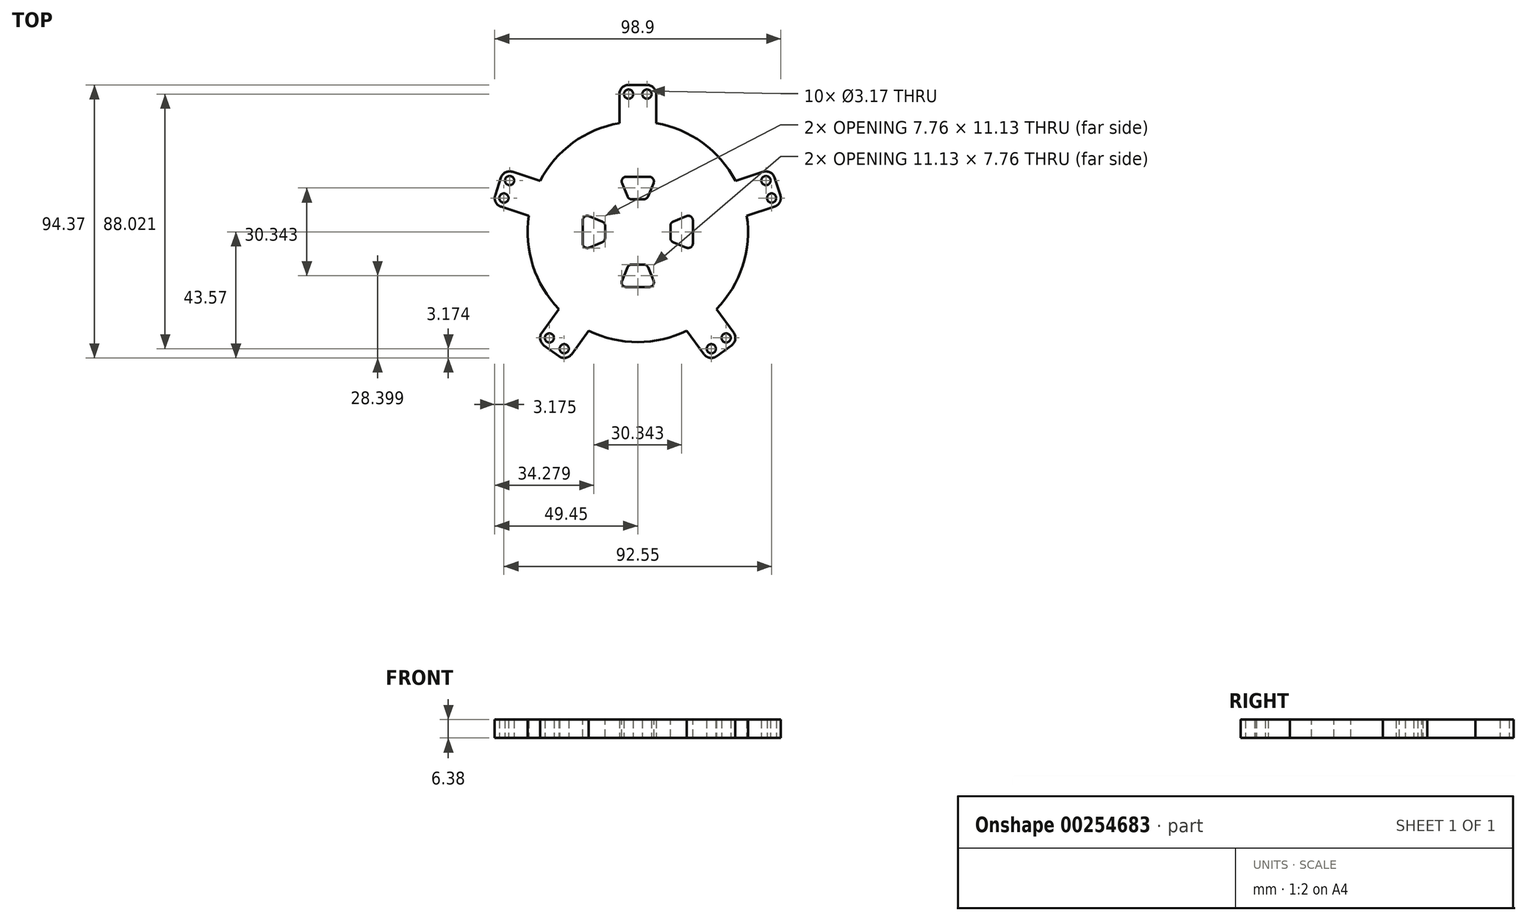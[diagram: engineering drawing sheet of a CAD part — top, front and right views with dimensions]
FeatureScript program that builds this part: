
annotation { "Feature Type Name" : "Feature", "Feature Type Description" : "" }
export const myFeature = defineFeature(function(context is Context, id is Id, definition is map)
    precondition{}
    {
        {
            var Q0;
            Q0=qCreatedBy(makeId("Top.planeOp"),FACE);
            var sketch = newSketch(context, id + "F0", { "sketchPlane" : qUnion([Q0])});
            skArc(sketch, "E0", {"start": v(-6.35, 37.57) * mm, "mid": v(-22.4, 30.82) * mm, "end": v(-33.77, 17.65) * mm});
            skLineSegment(sketch, "E1", {"start": v(0, 0) * mm, "end": v(0, 66.93) * mm, "construction": true});
            skLineSegment(sketch, "E2", {"start": v(-6.35, 37.57) * mm, "end": v(-6.35, 47.63) * mm});
            skLineSegment(sketch, "E3.MirrorCS", {"start": v(6.35, 37.57) * mm, "end": v(6.35, 47.63) * mm});
            skLineSegment(sketch, "E4", {"start": v(-3.18, 50.8) * mm, "end": v(3.18, 50.8) * mm});
            skCircle(sketch, "E5", {"center": v(-3.18, 47.63) * mm, "radius": 1.59 * mm});
            skCircle(sketch, "E6.MirrorC", {"center": v(3.18, 47.63) * mm, "radius": 1.59 * mm});
            skPoint(sketch, "E7.visualSharp", {"position": v(6.35, 50.8) * mm});
            skArc(sketch, "E7.filletArc", {"start": v(6.35, 47.63) * mm, "mid": v(5.42, 49.87) * mm, "end": v(3.18, 50.8) * mm});
            skPoint(sketch, "E8.visualSharp", {"position": v(-6.35, 50.8) * mm});
            skArc(sketch, "E8.filletArc", {"start": v(-3.18, 50.8) * mm, "mid": v(-5.42, 49.87) * mm, "end": v(-6.35, 47.63) * mm});
            skLineSegment(sketch, "E9.1.0", {"start": v(0, 0) * mm, "end": v(-63.65, 20.68) * mm, "construction": true});
            skLineSegment(sketch, "E9.1.1", {"start": v(-33.77, 17.65) * mm, "end": v(-43.33, 20.76) * mm});
            skPoint(sketch, "E9.1.2", {"position": v(-50.28, 9.66) * mm});
            skLineSegment(sketch, "E9.1.3", {"start": v(-49.3, 12.68) * mm, "end": v(-47.33, 18.72) * mm});
            skLineSegment(sketch, "E9.1.4", {"start": v(-37.7, 5.57) * mm, "end": v(-47.26, 8.68) * mm});
            skPoint(sketch, "E9.1.5", {"position": v(-46.35, 21.74) * mm});
            skArc(sketch, "E9.1.6", {"start": v(-43.33, 20.76) * mm, "mid": v(-45.75, 20.57) * mm, "end": v(-47.33, 18.72) * mm});
            skCircle(sketch, "E9.1.7", {"center": v(-44.31, 17.74) * mm, "radius": 1.59 * mm});
            skCircle(sketch, "E9.1.8", {"center": v(-46.28, 11.7) * mm, "radius": 1.59 * mm});
            skArc(sketch, "E9.1.9", {"start": v(-49.3, 12.68) * mm, "mid": v(-49.1, 10.26) * mm, "end": v(-47.26, 8.68) * mm});
            skLineSegment(sketch, "E9.2.0", {"start": v(0, 0) * mm, "end": v(-39.34, -54.15) * mm, "construction": true});
            skLineSegment(sketch, "E9.2.1", {"start": v(-27.22, -26.66) * mm, "end": v(-33.13, -34.8) * mm});
            skPoint(sketch, "E9.2.2", {"position": v(-24.72, -44.83) * mm});
            skLineSegment(sketch, "E9.2.3", {"start": v(-27.3, -42.96) * mm, "end": v(-32.43, -39.23) * mm});
            skLineSegment(sketch, "E9.2.4", {"start": v(-16.94, -34.12) * mm, "end": v(-22.86, -42.26) * mm});
            skPoint(sketch, "E9.2.5", {"position": v(-35, -37.37) * mm});
            skArc(sketch, "E9.2.6", {"start": v(-33.13, -34.8) * mm, "mid": v(-33.7, -37.16) * mm, "end": v(-32.43, -39.23) * mm});
            skCircle(sketch, "E9.2.7", {"center": v(-30.56, -36.66) * mm, "radius": 1.59 * mm});
            skCircle(sketch, "E9.2.8", {"center": v(-25.42, -40.4) * mm, "radius": 1.59 * mm});
            skArc(sketch, "E9.2.9", {"start": v(-27.3, -42.96) * mm, "mid": v(-24.93, -43.53) * mm, "end": v(-22.86, -42.26) * mm});
            skLineSegment(sketch, "E9.3.0", {"start": v(0, 0) * mm, "end": v(39.34, -54.15) * mm, "construction": true});
            skLineSegment(sketch, "E9.3.1", {"start": v(16.94, -34.12) * mm, "end": v(22.86, -42.26) * mm});
            skPoint(sketch, "E9.3.2", {"position": v(35, -37.37) * mm});
            skLineSegment(sketch, "E9.3.3", {"start": v(32.43, -39.23) * mm, "end": v(27.3, -42.96) * mm});
            skLineSegment(sketch, "E9.3.4", {"start": v(27.22, -26.66) * mm, "end": v(33.13, -34.8) * mm});
            skPoint(sketch, "E9.3.5", {"position": v(24.72, -44.83) * mm});
            skArc(sketch, "E9.3.6", {"start": v(22.86, -42.26) * mm, "mid": v(24.93, -43.53) * mm, "end": v(27.3, -42.96) * mm});
            skCircle(sketch, "E9.3.7", {"center": v(25.42, -40.4) * mm, "radius": 1.59 * mm});
            skCircle(sketch, "E9.3.8", {"center": v(30.56, -36.66) * mm, "radius": 1.59 * mm});
            skArc(sketch, "E9.3.9", {"start": v(32.43, -39.23) * mm, "mid": v(33.7, -37.16) * mm, "end": v(33.13, -34.8) * mm});
            skLineSegment(sketch, "E9.4.0", {"start": v(0, 0) * mm, "end": v(63.65, 20.68) * mm, "construction": true});
            skLineSegment(sketch, "E9.4.1", {"start": v(37.7, 5.57) * mm, "end": v(47.26, 8.68) * mm});
            skPoint(sketch, "E9.4.2", {"position": v(46.35, 21.74) * mm});
            skLineSegment(sketch, "E9.4.3", {"start": v(47.33, 18.72) * mm, "end": v(49.3, 12.68) * mm});
            skLineSegment(sketch, "E9.4.4", {"start": v(33.77, 17.65) * mm, "end": v(43.33, 20.76) * mm});
            skPoint(sketch, "E9.4.5", {"position": v(50.28, 9.66) * mm});
            skArc(sketch, "E9.4.6", {"start": v(47.26, 8.68) * mm, "mid": v(49.1, 10.26) * mm, "end": v(49.3, 12.68) * mm});
            skCircle(sketch, "E9.4.7", {"center": v(46.28, 11.7) * mm, "radius": 1.59 * mm});
            skCircle(sketch, "E9.4.8", {"center": v(44.31, 17.74) * mm, "radius": 1.59 * mm});
            skArc(sketch, "E9.4.9", {"start": v(47.33, 18.72) * mm, "mid": v(45.75, 20.57) * mm, "end": v(43.33, 20.76) * mm});
            skArc(sketch, "E10.trimOffspring", {"start": v(-37.7, 5.57) * mm, "mid": v(-36.24, -11.77) * mm, "end": v(-27.22, -26.66) * mm});
            skArc(sketch, "E11.trimOffspring", {"start": v(-16.94, -34.12) * mm, "mid": v(0, -38.1) * mm, "end": v(16.94, -34.12) * mm});
            skArc(sketch, "E12.trimOffspring", {"start": v(27.22, -26.66) * mm, "mid": v(36.24, -11.77) * mm, "end": v(37.7, 5.57) * mm});
            skArc(sketch, "E13.trimOffspring", {"start": v(33.77, 17.65) * mm, "mid": v(22.4, 30.82) * mm, "end": v(6.35, 37.57) * mm});
            skSolve(sketch);
        }
        {
            var Q0;
            Q0=makeQuery(id+"F0.imprint","IMPRINT",FACE,{"disambiguationData":[TD([[makeQuery(id+"F0.imprint","IMPRINT",EDGE,{"derivedFrom":sQuery(id+"F0.wireOp",EDGE,"E0")}),1.0]])]});
            extrude(context, id + "F1", {"entities" : qUnion([Q0]), "depth" : 6.38 * mm});
        }
        {
            var Q0;
            Q0=makeQuery(id+"F1.opExtrude","CAP_FACE",FACE,{"disambiguationData":[OSD([sQuery(id+"F0.wireOp",EDGE,"E0"),sQuery(id+"F0.wireOp",EDGE,"E2"),sQuery(id+"F0.wireOp",EDGE,"E3.MirrorCS"),sQuery(id+"F0.wireOp",EDGE,"E4"),sQuery(id+"F0.wireOp",EDGE,"E5"),sQuery(id+"F0.wireOp",EDGE,"E6.MirrorC"),sQuery(id+"F0.wireOp",EDGE,"E7.filletArc"),sQuery(id+"F0.wireOp",EDGE,"E8.filletArc"),sQuery(id+"F0.wireOp",EDGE,"E9.1.1"),sQuery(id+"F0.wireOp",EDGE,"E9.1.3"),sQuery(id+"F0.wireOp",EDGE,"E9.1.4"),sQuery(id+"F0.wireOp",EDGE,"E9.1.6"),sQuery(id+"F0.wireOp",EDGE,"E9.1.7"),sQuery(id+"F0.wireOp",EDGE,"E9.1.8"),sQuery(id+"F0.wireOp",EDGE,"E9.1.9"),sQuery(id+"F0.wireOp",EDGE,"E9.2.1"),sQuery(id+"F0.wireOp",EDGE,"E9.2.3"),sQuery(id+"F0.wireOp",EDGE,"E9.2.4"),sQuery(id+"F0.wireOp",EDGE,"E9.2.6"),sQuery(id+"F0.wireOp",EDGE,"E9.2.7"),sQuery(id+"F0.wireOp",EDGE,"E9.2.8"),sQuery(id+"F0.wireOp",EDGE,"E9.2.9"),sQuery(id+"F0.wireOp",EDGE,"E9.3.1"),sQuery(id+"F0.wireOp",EDGE,"E9.3.3"),sQuery(id+"F0.wireOp",EDGE,"E9.3.4"),sQuery(id+"F0.wireOp",EDGE,"E9.3.6"),sQuery(id+"F0.wireOp",EDGE,"E9.3.7"),sQuery(id+"F0.wireOp",EDGE,"E9.3.8"),sQuery(id+"F0.wireOp",EDGE,"E9.3.9"),sQuery(id+"F0.wireOp",EDGE,"E9.4.1"),sQuery(id+"F0.wireOp",EDGE,"E9.4.3"),sQuery(id+"F0.wireOp",EDGE,"E9.4.4"),sQuery(id+"F0.wireOp",EDGE,"E9.4.6"),sQuery(id+"F0.wireOp",EDGE,"E9.4.7"),sQuery(id+"F0.wireOp",EDGE,"E9.4.8"),sQuery(id+"F0.wireOp",EDGE,"E9.4.9"),sQuery(id+"F0.wireOp",EDGE,"E10.trimOffspring"),sQuery(id+"F0.wireOp",EDGE,"E11.trimOffspring"),sQuery(id+"F0.wireOp",EDGE,"E12.trimOffspring"),sQuery(id+"F0.wireOp",EDGE,"E13.trimOffspring")])],"isStart":false});
            var sketch = newSketch(context, id + "F2", { "sketchPlane" : qUnion([Q0])});
            skLineSegment(sketch, "E14", {"start": v(0, 0) * mm, "end": v(0, 38.1) * mm, "construction": true});
            skLineSegment(sketch, "E15", {"start": v(0, 19.05) * mm, "end": v(-3.98, 19.05) * mm});
            skLineSegment(sketch, "E16", {"start": v(-5.45, 16.86) * mm, "end": v(-3.58, 12.28) * mm});
            skLineSegment(sketch, "E17", {"start": v(-2.1, 11.3) * mm, "end": v(0, 11.3) * mm});
            skLineSegment(sketch, "E18.MirrorCS", {"start": v(0, 19.05) * mm, "end": v(3.98, 19.05) * mm});
            skLineSegment(sketch, "E19.MirrorCS", {"start": v(5.45, 16.86) * mm, "end": v(3.58, 12.28) * mm});
            skLineSegment(sketch, "E20.MirrorCS", {"start": v(2.1, 11.3) * mm, "end": v(0, 11.3) * mm});
            skPoint(sketch, "E21.visualSharp", {"position": v(-6.35, 19.05) * mm});
            skArc(sketch, "E21.filletArc", {"start": v(-3.98, 19.05) * mm, "mid": v(-5.3, 18.35) * mm, "end": v(-5.45, 16.86) * mm});
            skPoint(sketch, "E22.visualSharp", {"position": v(6.35, 19.05) * mm});
            skArc(sketch, "E22.filletArc", {"start": v(5.45, 16.86) * mm, "mid": v(5.3, 18.35) * mm, "end": v(3.98, 19.05) * mm});
            skPoint(sketch, "E23.visualSharp", {"position": v(3.17, 11.3) * mm});
            skArc(sketch, "E23.filletArc", {"start": v(2.1, 11.3) * mm, "mid": v(3, 11.56) * mm, "end": v(3.58, 12.28) * mm});
            skPoint(sketch, "E24.visualSharp", {"position": v(-3.18, 11.3) * mm});
            skArc(sketch, "E24.filletArc", {"start": v(-3.58, 12.28) * mm, "mid": v(-3, 11.56) * mm, "end": v(-2.1, 11.3) * mm});
            skLineSegment(sketch, "E25.1.0", {"start": v(-19.05, 0) * mm, "end": v(-19.05, -3.98) * mm});
            skLineSegment(sketch, "E25.1.1", {"start": v(-19.05, 0) * mm, "end": v(-19.05, 3.98) * mm});
            skArc(sketch, "E25.1.2", {"start": v(-16.86, 5.45) * mm, "mid": v(-18.35, 5.3) * mm, "end": v(-19.05, 3.98) * mm});
            skLineSegment(sketch, "E25.1.3", {"start": v(-16.86, 5.45) * mm, "end": v(-12.28, 3.58) * mm});
            skArc(sketch, "E25.1.4", {"start": v(-11.3, 2.1) * mm, "mid": v(-11.56, 3) * mm, "end": v(-12.28, 3.58) * mm});
            skLineSegment(sketch, "E25.1.5", {"start": v(-11.3, 2.1) * mm, "end": v(-11.3, 0) * mm});
            skLineSegment(sketch, "E25.1.6", {"start": v(-11.3, -2.1) * mm, "end": v(-11.3, 0) * mm});
            skArc(sketch, "E25.1.7", {"start": v(-12.28, -3.58) * mm, "mid": v(-11.56, -3) * mm, "end": v(-11.3, -2.1) * mm});
            skLineSegment(sketch, "E25.1.8", {"start": v(-16.86, -5.45) * mm, "end": v(-12.28, -3.58) * mm});
            skArc(sketch, "E25.1.9", {"start": v(-19.05, -3.98) * mm, "mid": v(-18.35, -5.3) * mm, "end": v(-16.86, -5.45) * mm});
            skLineSegment(sketch, "E25.2.0", {"start": v(0, -19.05) * mm, "end": v(3.98, -19.05) * mm});
            skLineSegment(sketch, "E25.2.1", {"start": v(0, -19.05) * mm, "end": v(-3.98, -19.05) * mm});
            skArc(sketch, "E25.2.2", {"start": v(-5.45, -16.86) * mm, "mid": v(-5.3, -18.35) * mm, "end": v(-3.98, -19.05) * mm});
            skLineSegment(sketch, "E25.2.3", {"start": v(-5.45, -16.86) * mm, "end": v(-3.58, -12.28) * mm});
            skArc(sketch, "E25.2.4", {"start": v(-2.1, -11.3) * mm, "mid": v(-3, -11.56) * mm, "end": v(-3.58, -12.28) * mm});
            skLineSegment(sketch, "E25.2.5", {"start": v(-2.1, -11.3) * mm, "end": v(0, -11.3) * mm});
            skLineSegment(sketch, "E25.2.6", {"start": v(2.1, -11.3) * mm, "end": v(0, -11.3) * mm});
            skArc(sketch, "E25.2.7", {"start": v(3.58, -12.28) * mm, "mid": v(3, -11.56) * mm, "end": v(2.1, -11.3) * mm});
            skLineSegment(sketch, "E25.2.8", {"start": v(5.45, -16.86) * mm, "end": v(3.58, -12.28) * mm});
            skArc(sketch, "E25.2.9", {"start": v(3.98, -19.05) * mm, "mid": v(5.3, -18.35) * mm, "end": v(5.45, -16.86) * mm});
            skLineSegment(sketch, "E25.3.0", {"start": v(19.05, 0) * mm, "end": v(19.05, 3.98) * mm});
            skLineSegment(sketch, "E25.3.1", {"start": v(19.05, 0) * mm, "end": v(19.05, -3.98) * mm});
            skArc(sketch, "E25.3.2", {"start": v(16.86, -5.45) * mm, "mid": v(18.35, -5.3) * mm, "end": v(19.05, -3.98) * mm});
            skLineSegment(sketch, "E25.3.3", {"start": v(16.86, -5.45) * mm, "end": v(12.28, -3.58) * mm});
            skArc(sketch, "E25.3.4", {"start": v(11.3, -2.1) * mm, "mid": v(11.56, -3) * mm, "end": v(12.28, -3.58) * mm});
            skLineSegment(sketch, "E25.3.5", {"start": v(11.3, -2.1) * mm, "end": v(11.3, 0) * mm});
            skLineSegment(sketch, "E25.3.6", {"start": v(11.3, 2.1) * mm, "end": v(11.3, 0) * mm});
            skArc(sketch, "E25.3.7", {"start": v(12.28, 3.58) * mm, "mid": v(11.56, 3) * mm, "end": v(11.3, 2.1) * mm});
            skLineSegment(sketch, "E25.3.8", {"start": v(16.86, 5.45) * mm, "end": v(12.28, 3.58) * mm});
            skArc(sketch, "E25.3.9", {"start": v(19.05, 3.98) * mm, "mid": v(18.35, 5.3) * mm, "end": v(16.86, 5.45) * mm});
            skPoint(sketch, "E25.center", {"position": v(0, 0) * mm});
            skSolve(sketch);
        }
        {
            var Q0;
            Q0=makeQuery(id+"F2.imprint","IMPRINT",FACE,{"disambiguationData":[TD([[makeQuery(id+"F2.imprint","IMPRINT",EDGE,{"derivedFrom":sQuery(id+"F2.wireOp",EDGE,"E15")}),1.0]])]});
            var Q1;
            Q1=makeQuery(id+"F2.imprint","IMPRINT",FACE,{"disambiguationData":[TD([[makeQuery(id+"F2.imprint","IMPRINT",EDGE,{"derivedFrom":sQuery(id+"F2.wireOp",EDGE,"E25.3.0")}),1.0]])]});
            var Q2;
            Q2=makeQuery(id+"F2.imprint","IMPRINT",FACE,{"disambiguationData":[TD([[makeQuery(id+"F2.imprint","IMPRINT",EDGE,{"derivedFrom":sQuery(id+"F2.wireOp",EDGE,"E25.2.0")}),1.0]])]});
            var Q3;
            Q3=makeQuery(id+"F2.imprint","IMPRINT",FACE,{"disambiguationData":[TD([[makeQuery(id+"F2.imprint","IMPRINT",EDGE,{"derivedFrom":sQuery(id+"F2.wireOp",EDGE,"E25.1.0")}),1.0]])]});
            extrude(context, id + "F3", {"entities" : qUnion([Q0, Q1, Q2, Q3]), "operationType" : NewBodyOperationType.REMOVE, "endBound" : BoundingType.THROUGH_ALL, "oppositeDirection" : true, "depth" : 25.4 * mm});
        }
    });
